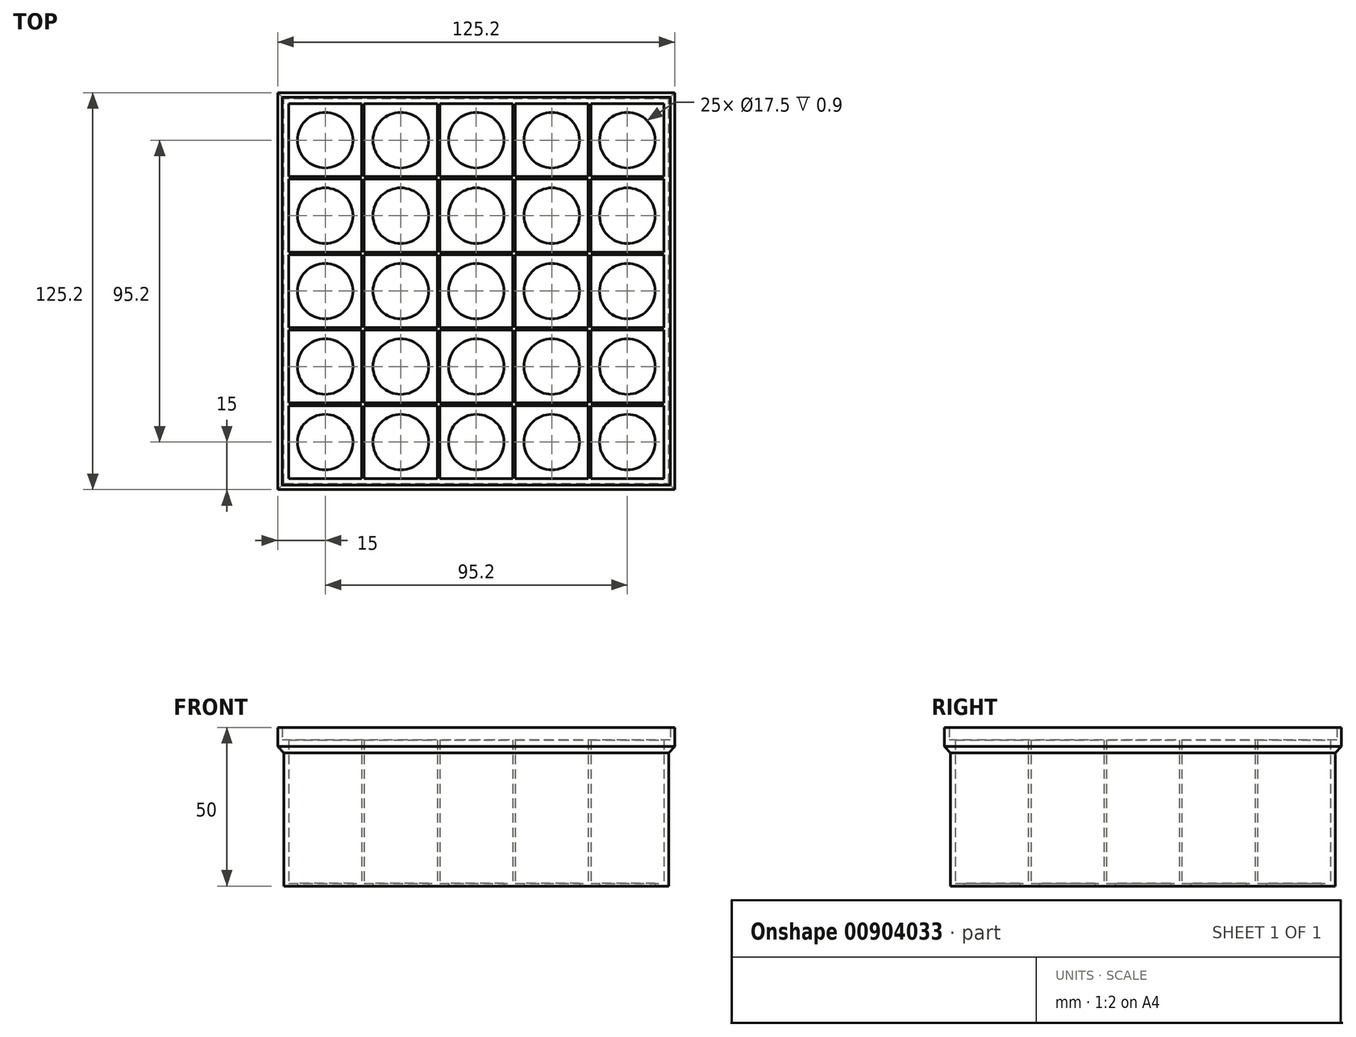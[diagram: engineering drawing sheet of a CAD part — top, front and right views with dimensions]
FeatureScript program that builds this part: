
annotation { "Feature Type Name" : "Feature", "Feature Type Description" : "" }
export const myFeature = defineFeature(function(context is Context, id is Id, definition is map)
    precondition{}
    {
        {
            var Q0;
            Q0=qCreatedBy(makeId("Top.planeOp"),FACE);
            var sketch = newSketch(context, id + "F0", { "sketchPlane" : qUnion([Q0])});
            skLineSegment(sketch, "E0.bottom", {"start": v(-60.6, 60.6) * mm, "end": v(60.6, 60.6) * mm});
            skLineSegment(sketch, "E0.top", {"start": v(-60.6, -60.6) * mm, "end": v(60.6, -60.6) * mm});
            skLineSegment(sketch, "E0.left", {"start": v(-60.6, 60.6) * mm, "end": v(-60.6, -60.6) * mm});
            skLineSegment(sketch, "E0.right", {"start": v(60.6, 60.6) * mm, "end": v(60.6, -60.6) * mm});
            skLineSegment(sketch, "E1", {"start": v(0, 51.44) * mm, "end": v(0, -51.44) * mm, "construction": true});
            skPoint(sketch, "E1.startSnap0", {"position": v(0, 60.6) * mm});
            skPoint(sketch, "E1.endSnap0", {"position": v(0, -60.6) * mm});
            skLineSegment(sketch, "E2", {"start": v(-71.19, 0) * mm, "end": v(76.63, 0) * mm, "construction": true});
            skPoint(sketch, "E2.startSnap0", {"position": v(-60.6, 0) * mm});
            skPoint(sketch, "E3", {"position": v(0, 0) * mm});
            skLineSegment(sketch, "E4", {"start": v(-59.1, 36.1) * mm, "end": v(-36.1, 36.1) * mm});
            skLineSegment(sketch, "E5", {"start": v(-36.1, 36.1) * mm, "end": v(-36.1, 59.1) * mm});
            skLineSegment(sketch, "E6", {"start": v(-59.1, 36.1) * mm, "end": v(-59.1, 59.1) * mm});
            skLineSegment(sketch, "E7", {"start": v(-59.1, 59.1) * mm, "end": v(-36.1, 59.1) * mm});
            skLineSegment(sketch, "E8", {"start": v(-36.1, 47.6) * mm, "end": v(-59.1, 47.6) * mm, "construction": true});
            skLineSegment(sketch, "E9", {"start": v(-47.6, 59.1) * mm, "end": v(-47.6, 36.1) * mm, "construction": true});
            skCircle(sketch, "E10", {"center": v(-47.6, 47.6) * mm, "radius": 8.75 * mm});
            skCircle(sketch, "E11.0.1.0", {"center": v(-47.6, 23.8) * mm, "radius": 8.75 * mm});
            skLineSegment(sketch, "E11.0.1.1", {"start": v(-59.1, 12.3) * mm, "end": v(-59.1, 35.3) * mm});
            skLineSegment(sketch, "E11.0.1.2", {"start": v(-59.1, 12.3) * mm, "end": v(-36.1, 12.3) * mm});
            skLineSegment(sketch, "E11.0.1.3", {"start": v(-59.1, 35.3) * mm, "end": v(-36.1, 35.3) * mm});
            skLineSegment(sketch, "E11.0.1.4", {"start": v(-47.6, 35.3) * mm, "end": v(-47.6, 12.3) * mm, "construction": true});
            skLineSegment(sketch, "E11.0.1.5", {"start": v(-36.1, 23.8) * mm, "end": v(-59.1, 23.8) * mm, "construction": true});
            skLineSegment(sketch, "E11.0.1.6", {"start": v(-36.1, 12.3) * mm, "end": v(-36.1, 35.3) * mm});
            skCircle(sketch, "E11.0.2.0", {"center": v(-47.6, 0) * mm, "radius": 8.75 * mm});
            skLineSegment(sketch, "E11.0.2.1", {"start": v(-59.1, -11.5) * mm, "end": v(-59.1, 11.5) * mm});
            skLineSegment(sketch, "E11.0.2.2", {"start": v(-59.1, -11.5) * mm, "end": v(-36.1, -11.5) * mm});
            skLineSegment(sketch, "E11.0.2.3", {"start": v(-59.1, 11.5) * mm, "end": v(-36.1, 11.5) * mm});
            skLineSegment(sketch, "E11.0.2.4", {"start": v(-47.6, 11.5) * mm, "end": v(-47.6, -11.5) * mm, "construction": true});
            skLineSegment(sketch, "E11.0.2.5", {"start": v(-36.1, 0) * mm, "end": v(-59.1, 0) * mm, "construction": true});
            skLineSegment(sketch, "E11.0.2.6", {"start": v(-36.1, -11.5) * mm, "end": v(-36.1, 11.5) * mm});
            skCircle(sketch, "E11.0.3.0", {"center": v(-47.6, -23.8) * mm, "radius": 8.75 * mm});
            skLineSegment(sketch, "E11.0.3.1", {"start": v(-59.1, -35.3) * mm, "end": v(-59.1, -12.3) * mm});
            skLineSegment(sketch, "E11.0.3.2", {"start": v(-59.1, -35.3) * mm, "end": v(-36.1, -35.3) * mm});
            skLineSegment(sketch, "E11.0.3.3", {"start": v(-59.1, -12.3) * mm, "end": v(-36.1, -12.3) * mm});
            skLineSegment(sketch, "E11.0.3.4", {"start": v(-47.6, -12.3) * mm, "end": v(-47.6, -35.3) * mm, "construction": true});
            skLineSegment(sketch, "E11.0.3.5", {"start": v(-36.1, -23.8) * mm, "end": v(-59.1, -23.8) * mm, "construction": true});
            skLineSegment(sketch, "E11.0.3.6", {"start": v(-36.1, -35.3) * mm, "end": v(-36.1, -12.3) * mm});
            skCircle(sketch, "E11.0.4.0", {"center": v(-47.6, -47.6) * mm, "radius": 8.75 * mm});
            skLineSegment(sketch, "E11.0.4.1", {"start": v(-59.1, -59.1) * mm, "end": v(-59.1, -36.1) * mm});
            skLineSegment(sketch, "E11.0.4.2", {"start": v(-59.1, -59.1) * mm, "end": v(-36.1, -59.1) * mm});
            skLineSegment(sketch, "E11.0.4.3", {"start": v(-59.1, -36.1) * mm, "end": v(-36.1, -36.1) * mm});
            skLineSegment(sketch, "E11.0.4.4", {"start": v(-47.6, -36.1) * mm, "end": v(-47.6, -59.1) * mm, "construction": true});
            skLineSegment(sketch, "E11.0.4.5", {"start": v(-36.1, -47.6) * mm, "end": v(-59.1, -47.6) * mm, "construction": true});
            skLineSegment(sketch, "E11.0.4.6", {"start": v(-36.1, -59.1) * mm, "end": v(-36.1, -36.1) * mm});
            skCircle(sketch, "E11.1.0.0", {"center": v(-23.8, 47.6) * mm, "radius": 8.75 * mm});
            skLineSegment(sketch, "E11.1.0.1", {"start": v(-35.3, 36.1) * mm, "end": v(-35.3, 59.1) * mm});
            skLineSegment(sketch, "E11.1.0.2", {"start": v(-35.3, 36.1) * mm, "end": v(-12.3, 36.1) * mm});
            skLineSegment(sketch, "E11.1.0.3", {"start": v(-35.3, 59.1) * mm, "end": v(-12.3, 59.1) * mm});
            skLineSegment(sketch, "E11.1.0.4", {"start": v(-23.8, 59.1) * mm, "end": v(-23.8, 36.1) * mm, "construction": true});
            skLineSegment(sketch, "E11.1.0.5", {"start": v(-12.3, 47.6) * mm, "end": v(-35.3, 47.6) * mm, "construction": true});
            skLineSegment(sketch, "E11.1.0.6", {"start": v(-12.3, 36.1) * mm, "end": v(-12.3, 59.1) * mm});
            skCircle(sketch, "E11.1.1.0", {"center": v(-23.8, 23.8) * mm, "radius": 8.75 * mm});
            skLineSegment(sketch, "E11.1.1.1", {"start": v(-35.3, 12.3) * mm, "end": v(-35.3, 35.3) * mm});
            skLineSegment(sketch, "E11.1.1.2", {"start": v(-35.3, 12.3) * mm, "end": v(-12.3, 12.3) * mm});
            skLineSegment(sketch, "E11.1.1.3", {"start": v(-35.3, 35.3) * mm, "end": v(-12.3, 35.3) * mm});
            skLineSegment(sketch, "E11.1.1.4", {"start": v(-23.8, 35.3) * mm, "end": v(-23.8, 12.3) * mm, "construction": true});
            skLineSegment(sketch, "E11.1.1.5", {"start": v(-12.3, 23.8) * mm, "end": v(-35.3, 23.8) * mm, "construction": true});
            skLineSegment(sketch, "E11.1.1.6", {"start": v(-12.3, 12.3) * mm, "end": v(-12.3, 35.3) * mm});
            skCircle(sketch, "E11.1.2.0", {"center": v(-23.8, 0) * mm, "radius": 8.75 * mm});
            skLineSegment(sketch, "E11.1.2.1", {"start": v(-35.3, -11.5) * mm, "end": v(-35.3, 11.5) * mm});
            skLineSegment(sketch, "E11.1.2.2", {"start": v(-35.3, -11.5) * mm, "end": v(-12.3, -11.5) * mm});
            skLineSegment(sketch, "E11.1.2.3", {"start": v(-35.3, 11.5) * mm, "end": v(-12.3, 11.5) * mm});
            skLineSegment(sketch, "E11.1.2.4", {"start": v(-23.8, 11.5) * mm, "end": v(-23.8, -11.5) * mm, "construction": true});
            skLineSegment(sketch, "E11.1.2.5", {"start": v(-12.3, 0) * mm, "end": v(-35.3, 0) * mm, "construction": true});
            skLineSegment(sketch, "E11.1.2.6", {"start": v(-12.3, -11.5) * mm, "end": v(-12.3, 11.5) * mm});
            skCircle(sketch, "E11.1.3.0", {"center": v(-23.8, -23.8) * mm, "radius": 8.75 * mm});
            skLineSegment(sketch, "E11.1.3.1", {"start": v(-35.3, -35.3) * mm, "end": v(-35.3, -12.3) * mm});
            skLineSegment(sketch, "E11.1.3.2", {"start": v(-35.3, -35.3) * mm, "end": v(-12.3, -35.3) * mm});
            skLineSegment(sketch, "E11.1.3.3", {"start": v(-35.3, -12.3) * mm, "end": v(-12.3, -12.3) * mm});
            skLineSegment(sketch, "E11.1.3.4", {"start": v(-23.8, -12.3) * mm, "end": v(-23.8, -35.3) * mm, "construction": true});
            skLineSegment(sketch, "E11.1.3.5", {"start": v(-12.3, -23.8) * mm, "end": v(-35.3, -23.8) * mm, "construction": true});
            skLineSegment(sketch, "E11.1.3.6", {"start": v(-12.3, -35.3) * mm, "end": v(-12.3, -12.3) * mm});
            skCircle(sketch, "E11.1.4.0", {"center": v(-23.8, -47.6) * mm, "radius": 8.75 * mm});
            skLineSegment(sketch, "E11.1.4.1", {"start": v(-35.3, -59.1) * mm, "end": v(-35.3, -36.1) * mm});
            skLineSegment(sketch, "E11.1.4.2", {"start": v(-35.3, -59.1) * mm, "end": v(-12.3, -59.1) * mm});
            skLineSegment(sketch, "E11.1.4.3", {"start": v(-35.3, -36.1) * mm, "end": v(-12.3, -36.1) * mm});
            skLineSegment(sketch, "E11.1.4.4", {"start": v(-23.8, -36.1) * mm, "end": v(-23.8, -59.1) * mm, "construction": true});
            skLineSegment(sketch, "E11.1.4.5", {"start": v(-12.3, -47.6) * mm, "end": v(-35.3, -47.6) * mm, "construction": true});
            skLineSegment(sketch, "E11.1.4.6", {"start": v(-12.3, -59.1) * mm, "end": v(-12.3, -36.1) * mm});
            skCircle(sketch, "E11.2.0.0", {"center": v(0, 47.6) * mm, "radius": 8.75 * mm});
            skLineSegment(sketch, "E11.2.0.1", {"start": v(-11.5, 36.1) * mm, "end": v(-11.5, 59.1) * mm});
            skLineSegment(sketch, "E11.2.0.2", {"start": v(-11.5, 36.1) * mm, "end": v(11.5, 36.1) * mm});
            skLineSegment(sketch, "E11.2.0.3", {"start": v(-11.5, 59.1) * mm, "end": v(11.5, 59.1) * mm});
            skLineSegment(sketch, "E11.2.0.4", {"start": v(0, 59.1) * mm, "end": v(0, 36.1) * mm, "construction": true});
            skLineSegment(sketch, "E11.2.0.5", {"start": v(11.5, 47.6) * mm, "end": v(-11.5, 47.6) * mm, "construction": true});
            skLineSegment(sketch, "E11.2.0.6", {"start": v(11.5, 36.1) * mm, "end": v(11.5, 59.1) * mm});
            skCircle(sketch, "E11.2.1.0", {"center": v(0, 23.8) * mm, "radius": 8.75 * mm});
            skLineSegment(sketch, "E11.2.1.1", {"start": v(-11.5, 12.3) * mm, "end": v(-11.5, 35.3) * mm});
            skLineSegment(sketch, "E11.2.1.2", {"start": v(-11.5, 12.3) * mm, "end": v(11.5, 12.3) * mm});
            skLineSegment(sketch, "E11.2.1.3", {"start": v(-11.5, 35.3) * mm, "end": v(11.5, 35.3) * mm});
            skLineSegment(sketch, "E11.2.1.4", {"start": v(0, 35.3) * mm, "end": v(0, 12.3) * mm, "construction": true});
            skLineSegment(sketch, "E11.2.1.5", {"start": v(11.5, 23.8) * mm, "end": v(-11.5, 23.8) * mm, "construction": true});
            skLineSegment(sketch, "E11.2.1.6", {"start": v(11.5, 12.3) * mm, "end": v(11.5, 35.3) * mm});
            skCircle(sketch, "E11.2.2.0", {"center": v(0, 0) * mm, "radius": 8.75 * mm});
            skLineSegment(sketch, "E11.2.2.1", {"start": v(-11.5, -11.5) * mm, "end": v(-11.5, 11.5) * mm});
            skLineSegment(sketch, "E11.2.2.2", {"start": v(-11.5, -11.5) * mm, "end": v(11.5, -11.5) * mm});
            skLineSegment(sketch, "E11.2.2.3", {"start": v(-11.5, 11.5) * mm, "end": v(11.5, 11.5) * mm});
            skLineSegment(sketch, "E11.2.2.4", {"start": v(0, 11.5) * mm, "end": v(0, -11.5) * mm, "construction": true});
            skLineSegment(sketch, "E11.2.2.5", {"start": v(11.5, 0) * mm, "end": v(-11.5, 0) * mm, "construction": true});
            skLineSegment(sketch, "E11.2.2.6", {"start": v(11.5, -11.5) * mm, "end": v(11.5, 11.5) * mm});
            skCircle(sketch, "E11.2.3.0", {"center": v(0, -23.8) * mm, "radius": 8.75 * mm});
            skLineSegment(sketch, "E11.2.3.1", {"start": v(-11.5, -35.3) * mm, "end": v(-11.5, -12.3) * mm});
            skLineSegment(sketch, "E11.2.3.2", {"start": v(-11.5, -35.3) * mm, "end": v(11.5, -35.3) * mm});
            skLineSegment(sketch, "E11.2.3.3", {"start": v(-11.5, -12.3) * mm, "end": v(11.5, -12.3) * mm});
            skLineSegment(sketch, "E11.2.3.4", {"start": v(0, -12.3) * mm, "end": v(0, -35.3) * mm, "construction": true});
            skLineSegment(sketch, "E11.2.3.5", {"start": v(11.5, -23.8) * mm, "end": v(-11.5, -23.8) * mm, "construction": true});
            skLineSegment(sketch, "E11.2.3.6", {"start": v(11.5, -35.3) * mm, "end": v(11.5, -12.3) * mm});
            skCircle(sketch, "E11.2.4.0", {"center": v(0, -47.6) * mm, "radius": 8.75 * mm});
            skLineSegment(sketch, "E11.2.4.1", {"start": v(-11.5, -59.1) * mm, "end": v(-11.5, -36.1) * mm});
            skLineSegment(sketch, "E11.2.4.2", {"start": v(-11.5, -59.1) * mm, "end": v(11.5, -59.1) * mm});
            skLineSegment(sketch, "E11.2.4.3", {"start": v(-11.5, -36.1) * mm, "end": v(11.5, -36.1) * mm});
            skLineSegment(sketch, "E11.2.4.4", {"start": v(0, -36.1) * mm, "end": v(0, -59.1) * mm, "construction": true});
            skLineSegment(sketch, "E11.2.4.5", {"start": v(11.5, -47.6) * mm, "end": v(-11.5, -47.6) * mm, "construction": true});
            skLineSegment(sketch, "E11.2.4.6", {"start": v(11.5, -59.1) * mm, "end": v(11.5, -36.1) * mm});
            skCircle(sketch, "E11.3.0.0", {"center": v(23.8, 47.6) * mm, "radius": 8.75 * mm});
            skLineSegment(sketch, "E11.3.0.1", {"start": v(12.3, 36.1) * mm, "end": v(12.3, 59.1) * mm});
            skLineSegment(sketch, "E11.3.0.2", {"start": v(12.3, 36.1) * mm, "end": v(35.3, 36.1) * mm});
            skLineSegment(sketch, "E11.3.0.3", {"start": v(12.3, 59.1) * mm, "end": v(35.3, 59.1) * mm});
            skLineSegment(sketch, "E11.3.0.4", {"start": v(23.8, 59.1) * mm, "end": v(23.8, 36.1) * mm, "construction": true});
            skLineSegment(sketch, "E11.3.0.5", {"start": v(35.3, 47.6) * mm, "end": v(12.3, 47.6) * mm, "construction": true});
            skLineSegment(sketch, "E11.3.0.6", {"start": v(35.3, 36.1) * mm, "end": v(35.3, 59.1) * mm});
            skCircle(sketch, "E11.3.1.0", {"center": v(23.8, 23.8) * mm, "radius": 8.75 * mm});
            skLineSegment(sketch, "E11.3.1.1", {"start": v(12.3, 12.3) * mm, "end": v(12.3, 35.3) * mm});
            skLineSegment(sketch, "E11.3.1.2", {"start": v(12.3, 12.3) * mm, "end": v(35.3, 12.3) * mm});
            skLineSegment(sketch, "E11.3.1.3", {"start": v(12.3, 35.3) * mm, "end": v(35.3, 35.3) * mm});
            skLineSegment(sketch, "E11.3.1.4", {"start": v(23.8, 35.3) * mm, "end": v(23.8, 12.3) * mm, "construction": true});
            skLineSegment(sketch, "E11.3.1.5", {"start": v(35.3, 23.8) * mm, "end": v(12.3, 23.8) * mm, "construction": true});
            skLineSegment(sketch, "E11.3.1.6", {"start": v(35.3, 12.3) * mm, "end": v(35.3, 35.3) * mm});
            skCircle(sketch, "E11.3.2.0", {"center": v(23.8, 0) * mm, "radius": 8.75 * mm});
            skLineSegment(sketch, "E11.3.2.1", {"start": v(12.3, -11.5) * mm, "end": v(12.3, 11.5) * mm});
            skLineSegment(sketch, "E11.3.2.2", {"start": v(12.3, -11.5) * mm, "end": v(35.3, -11.5) * mm});
            skLineSegment(sketch, "E11.3.2.3", {"start": v(12.3, 11.5) * mm, "end": v(35.3, 11.5) * mm});
            skLineSegment(sketch, "E11.3.2.4", {"start": v(23.8, 11.5) * mm, "end": v(23.8, -11.5) * mm, "construction": true});
            skLineSegment(sketch, "E11.3.2.5", {"start": v(35.3, 0) * mm, "end": v(12.3, 0) * mm, "construction": true});
            skLineSegment(sketch, "E11.3.2.6", {"start": v(35.3, -11.5) * mm, "end": v(35.3, 11.5) * mm});
            skCircle(sketch, "E11.3.3.0", {"center": v(23.8, -23.8) * mm, "radius": 8.75 * mm});
            skLineSegment(sketch, "E11.3.3.1", {"start": v(12.3, -35.3) * mm, "end": v(12.3, -12.3) * mm});
            skLineSegment(sketch, "E11.3.3.2", {"start": v(12.3, -35.3) * mm, "end": v(35.3, -35.3) * mm});
            skLineSegment(sketch, "E11.3.3.3", {"start": v(12.3, -12.3) * mm, "end": v(35.3, -12.3) * mm});
            skLineSegment(sketch, "E11.3.3.4", {"start": v(23.8, -12.3) * mm, "end": v(23.8, -35.3) * mm, "construction": true});
            skLineSegment(sketch, "E11.3.3.5", {"start": v(35.3, -23.8) * mm, "end": v(12.3, -23.8) * mm, "construction": true});
            skLineSegment(sketch, "E11.3.3.6", {"start": v(35.3, -35.3) * mm, "end": v(35.3, -12.3) * mm});
            skCircle(sketch, "E11.3.4.0", {"center": v(23.8, -47.6) * mm, "radius": 8.75 * mm});
            skLineSegment(sketch, "E11.3.4.1", {"start": v(12.3, -59.1) * mm, "end": v(12.3, -36.1) * mm});
            skLineSegment(sketch, "E11.3.4.2", {"start": v(12.3, -59.1) * mm, "end": v(35.3, -59.1) * mm});
            skLineSegment(sketch, "E11.3.4.3", {"start": v(12.3, -36.1) * mm, "end": v(35.3, -36.1) * mm});
            skLineSegment(sketch, "E11.3.4.4", {"start": v(23.8, -36.1) * mm, "end": v(23.8, -59.1) * mm, "construction": true});
            skLineSegment(sketch, "E11.3.4.5", {"start": v(35.3, -47.6) * mm, "end": v(12.3, -47.6) * mm, "construction": true});
            skLineSegment(sketch, "E11.3.4.6", {"start": v(35.3, -59.1) * mm, "end": v(35.3, -36.1) * mm});
            skCircle(sketch, "E11.4.0.0", {"center": v(47.6, 47.6) * mm, "radius": 8.75 * mm});
            skLineSegment(sketch, "E11.4.0.1", {"start": v(36.1, 36.1) * mm, "end": v(36.1, 59.1) * mm});
            skLineSegment(sketch, "E11.4.0.2", {"start": v(36.1, 36.1) * mm, "end": v(59.1, 36.1) * mm});
            skLineSegment(sketch, "E11.4.0.3", {"start": v(36.1, 59.1) * mm, "end": v(59.1, 59.1) * mm});
            skLineSegment(sketch, "E11.4.0.4", {"start": v(47.6, 59.1) * mm, "end": v(47.6, 36.1) * mm, "construction": true});
            skLineSegment(sketch, "E11.4.0.5", {"start": v(59.1, 47.6) * mm, "end": v(36.1, 47.6) * mm, "construction": true});
            skLineSegment(sketch, "E11.4.0.6", {"start": v(59.1, 36.1) * mm, "end": v(59.1, 59.1) * mm});
            skCircle(sketch, "E11.4.1.0", {"center": v(47.6, 23.8) * mm, "radius": 8.75 * mm});
            skLineSegment(sketch, "E11.4.1.1", {"start": v(36.1, 12.3) * mm, "end": v(36.1, 35.3) * mm});
            skLineSegment(sketch, "E11.4.1.2", {"start": v(36.1, 12.3) * mm, "end": v(59.1, 12.3) * mm});
            skLineSegment(sketch, "E11.4.1.3", {"start": v(36.1, 35.3) * mm, "end": v(59.1, 35.3) * mm});
            skLineSegment(sketch, "E11.4.1.4", {"start": v(47.6, 35.3) * mm, "end": v(47.6, 12.3) * mm, "construction": true});
            skLineSegment(sketch, "E11.4.1.5", {"start": v(59.1, 23.8) * mm, "end": v(36.1, 23.8) * mm, "construction": true});
            skLineSegment(sketch, "E11.4.1.6", {"start": v(59.1, 12.3) * mm, "end": v(59.1, 35.3) * mm});
            skCircle(sketch, "E11.4.2.0", {"center": v(47.6, 0) * mm, "radius": 8.75 * mm});
            skLineSegment(sketch, "E11.4.2.1", {"start": v(36.1, -11.5) * mm, "end": v(36.1, 11.5) * mm});
            skLineSegment(sketch, "E11.4.2.2", {"start": v(36.1, -11.5) * mm, "end": v(59.1, -11.5) * mm});
            skLineSegment(sketch, "E11.4.2.3", {"start": v(36.1, 11.5) * mm, "end": v(59.1, 11.5) * mm});
            skLineSegment(sketch, "E11.4.2.4", {"start": v(47.6, 11.5) * mm, "end": v(47.6, -11.5) * mm, "construction": true});
            skLineSegment(sketch, "E11.4.2.5", {"start": v(59.1, 0) * mm, "end": v(36.1, 0) * mm, "construction": true});
            skLineSegment(sketch, "E11.4.2.6", {"start": v(59.1, -11.5) * mm, "end": v(59.1, 11.5) * mm});
            skCircle(sketch, "E11.4.3.0", {"center": v(47.6, -23.8) * mm, "radius": 8.75 * mm});
            skLineSegment(sketch, "E11.4.3.1", {"start": v(36.1, -35.3) * mm, "end": v(36.1, -12.3) * mm});
            skLineSegment(sketch, "E11.4.3.2", {"start": v(36.1, -35.3) * mm, "end": v(59.1, -35.3) * mm});
            skLineSegment(sketch, "E11.4.3.3", {"start": v(36.1, -12.3) * mm, "end": v(59.1, -12.3) * mm});
            skLineSegment(sketch, "E11.4.3.4", {"start": v(47.6, -12.3) * mm, "end": v(47.6, -35.3) * mm, "construction": true});
            skLineSegment(sketch, "E11.4.3.5", {"start": v(59.1, -23.8) * mm, "end": v(36.1, -23.8) * mm, "construction": true});
            skLineSegment(sketch, "E11.4.3.6", {"start": v(59.1, -35.3) * mm, "end": v(59.1, -12.3) * mm});
            skCircle(sketch, "E11.4.4.0", {"center": v(47.6, -47.6) * mm, "radius": 8.75 * mm});
            skLineSegment(sketch, "E11.4.4.1", {"start": v(36.1, -59.1) * mm, "end": v(36.1, -36.1) * mm});
            skLineSegment(sketch, "E11.4.4.2", {"start": v(36.1, -59.1) * mm, "end": v(59.1, -59.1) * mm});
            skLineSegment(sketch, "E11.4.4.3", {"start": v(36.1, -36.1) * mm, "end": v(59.1, -36.1) * mm});
            skLineSegment(sketch, "E11.4.4.4", {"start": v(47.6, -36.1) * mm, "end": v(47.6, -59.1) * mm, "construction": true});
            skLineSegment(sketch, "E11.4.4.5", {"start": v(59.1, -47.6) * mm, "end": v(36.1, -47.6) * mm, "construction": true});
            skLineSegment(sketch, "E11.4.4.6", {"start": v(59.1, -59.1) * mm, "end": v(59.1, -36.1) * mm});
            skLineSegment(sketch, "E11.direction1", {"start": v(-59.1, 36.1) * mm, "end": v(-35.3, 36.1) * mm, "construction": true});
            skLineSegment(sketch, "E11.direction2", {"start": v(-59.1, 36.1) * mm, "end": v(-59.1, 12.3) * mm, "construction": true});
            skLineSegment(sketch, "E12", {"start": v(-59.1, 36.1) * mm, "end": v(-59.1, 35.3) * mm});
            skLineSegment(sketch, "E13", {"start": v(-59.1, 12.3) * mm, "end": v(-59.1, 11.5) * mm});
            skLineSegment(sketch, "E14", {"start": v(-59.1, -11.5) * mm, "end": v(-59.1, -12.3) * mm});
            skLineSegment(sketch, "E15", {"start": v(-59.1, -35.3) * mm, "end": v(-59.1, -36.1) * mm});
            skLineSegment(sketch, "E16", {"start": v(-36.1, -59.1) * mm, "end": v(-35.3, -59.1) * mm});
            skLineSegment(sketch, "E17", {"start": v(-12.3, -59.1) * mm, "end": v(-11.5, -59.1) * mm});
            skLineSegment(sketch, "E18", {"start": v(11.5, -59.1) * mm, "end": v(12.3, -59.1) * mm});
            skLineSegment(sketch, "E19", {"start": v(35.3, -59.1) * mm, "end": v(36.1, -59.1) * mm});
            skLineSegment(sketch, "E20", {"start": v(59.1, -36.1) * mm, "end": v(59.1, -35.3) * mm});
            skLineSegment(sketch, "E21", {"start": v(59.1, -12.3) * mm, "end": v(59.1, -11.5) * mm});
            skLineSegment(sketch, "E22", {"start": v(59.1, 11.5) * mm, "end": v(59.1, 12.3) * mm});
            skLineSegment(sketch, "E23", {"start": v(59.1, 35.3) * mm, "end": v(59.1, 36.1) * mm});
            skLineSegment(sketch, "E24", {"start": v(35.3, 59.1) * mm, "end": v(36.1, 59.1) * mm});
            skLineSegment(sketch, "E25", {"start": v(11.5, 59.1) * mm, "end": v(12.3, 59.1) * mm});
            skLineSegment(sketch, "E26", {"start": v(-12.3, 59.1) * mm, "end": v(-11.5, 59.1) * mm});
            skLineSegment(sketch, "E27", {"start": v(-36.1, 59.1) * mm, "end": v(-35.3, 59.1) * mm});
            skSolve(sketch);
        }
        {
            var Q0;
            Q0=makeQuery(id+"F0.imprint","IMPRINT",FACE,{"disambiguationData":[TD([[makeQuery(id+"F0.imprint","IMPRINT",EDGE,{"derivedFrom":sQuery(id+"F0.wireOp",EDGE,"E4")}),-1.0]])]});
            var Q1;
            Q1=makeQuery(id+"F0.imprint","IMPRINT",FACE,{"disambiguationData":[TD([[makeQuery(id+"F0.imprint","IMPRINT",EDGE,{"derivedFrom":sQuery(id+"F0.wireOp",EDGE,"E0.bottom")}),-1.0]])]});
            extrude(context, id + "F1", {"entities" : qUnion([Q0, Q1]), "depth" : 46 * mm, "offsetDistance" : 25 * mm});
        }
        {
            var Q0;
            Q0=makeQuery(id+"F0.imprint","IMPRINT",FACE,{"disambiguationData":[TD([[makeQuery(id+"F0.imprint","IMPRINT",EDGE,{"derivedFrom":sQuery(id+"F0.wireOp",EDGE,"E4")}),1.0]])]});
            var Q1;
            Q1=makeQuery(id+"F0.imprint","IMPRINT",FACE,{"disambiguationData":[TD([[makeQuery(id+"F0.imprint","IMPRINT",EDGE,{"derivedFrom":sQuery(id+"F0.wireOp",EDGE,"E11.1.0.0")}),-1.0]])]});
            var Q2;
            Q2=makeQuery(id+"F0.imprint","IMPRINT",FACE,{"disambiguationData":[TD([[makeQuery(id+"F0.imprint","IMPRINT",EDGE,{"derivedFrom":sQuery(id+"F0.wireOp",EDGE,"E11.2.0.0")}),-1.0]])]});
            var Q3;
            Q3=makeQuery(id+"F0.imprint","IMPRINT",FACE,{"disambiguationData":[TD([[makeQuery(id+"F0.imprint","IMPRINT",EDGE,{"derivedFrom":sQuery(id+"F0.wireOp",EDGE,"E11.3.0.0")}),-1.0]])]});
            var Q4;
            Q4=makeQuery(id+"F0.imprint","IMPRINT",FACE,{"disambiguationData":[TD([[makeQuery(id+"F0.imprint","IMPRINT",EDGE,{"derivedFrom":sQuery(id+"F0.wireOp",EDGE,"E11.4.0.0")}),-1.0]])]});
            var Q5;
            Q5=makeQuery(id+"F0.imprint","IMPRINT",FACE,{"disambiguationData":[TD([[makeQuery(id+"F0.imprint","IMPRINT",EDGE,{"derivedFrom":sQuery(id+"F0.wireOp",EDGE,"E11.4.1.0")}),-1.0]])]});
            var Q6;
            Q6=makeQuery(id+"F0.imprint","IMPRINT",FACE,{"disambiguationData":[TD([[makeQuery(id+"F0.imprint","IMPRINT",EDGE,{"derivedFrom":sQuery(id+"F0.wireOp",EDGE,"E11.3.1.0")}),-1.0]])]});
            var Q7;
            Q7=makeQuery(id+"F0.imprint","IMPRINT",FACE,{"disambiguationData":[TD([[makeQuery(id+"F0.imprint","IMPRINT",EDGE,{"derivedFrom":sQuery(id+"F0.wireOp",EDGE,"E11.2.1.0")}),-1.0]])]});
            var Q8;
            Q8=makeQuery(id+"F0.imprint","IMPRINT",FACE,{"disambiguationData":[TD([[makeQuery(id+"F0.imprint","IMPRINT",EDGE,{"derivedFrom":sQuery(id+"F0.wireOp",EDGE,"E11.1.1.0")}),-1.0]])]});
            var Q9;
            Q9=makeQuery(id+"F0.imprint","IMPRINT",FACE,{"disambiguationData":[TD([[makeQuery(id+"F0.imprint","IMPRINT",EDGE,{"derivedFrom":sQuery(id+"F0.wireOp",EDGE,"E11.0.1.0")}),-1.0]])]});
            var Q10;
            Q10=makeQuery(id+"F0.imprint","IMPRINT",FACE,{"disambiguationData":[TD([[makeQuery(id+"F0.imprint","IMPRINT",EDGE,{"derivedFrom":sQuery(id+"F0.wireOp",EDGE,"E11.0.2.0")}),-1.0]])]});
            var Q11;
            Q11=makeQuery(id+"F0.imprint","IMPRINT",FACE,{"disambiguationData":[TD([[makeQuery(id+"F0.imprint","IMPRINT",EDGE,{"derivedFrom":sQuery(id+"F0.wireOp",EDGE,"E11.1.2.0")}),-1.0]])]});
            var Q12;
            Q12=makeQuery(id+"F0.imprint","IMPRINT",FACE,{"disambiguationData":[TD([[makeQuery(id+"F0.imprint","IMPRINT",EDGE,{"derivedFrom":sQuery(id+"F0.wireOp",EDGE,"E11.2.2.0")}),-1.0]])]});
            var Q13;
            Q13=makeQuery(id+"F0.imprint","IMPRINT",FACE,{"disambiguationData":[TD([[makeQuery(id+"F0.imprint","IMPRINT",EDGE,{"derivedFrom":sQuery(id+"F0.wireOp",EDGE,"E11.3.2.0")}),-1.0]])]});
            var Q14;
            Q14=makeQuery(id+"F0.imprint","IMPRINT",FACE,{"disambiguationData":[TD([[makeQuery(id+"F0.imprint","IMPRINT",EDGE,{"derivedFrom":sQuery(id+"F0.wireOp",EDGE,"E11.4.2.0")}),-1.0]])]});
            var Q15;
            Q15=makeQuery(id+"F0.imprint","IMPRINT",FACE,{"disambiguationData":[TD([[makeQuery(id+"F0.imprint","IMPRINT",EDGE,{"derivedFrom":sQuery(id+"F0.wireOp",EDGE,"E11.4.3.0")}),-1.0]])]});
            var Q16;
            Q16=makeQuery(id+"F0.imprint","IMPRINT",FACE,{"disambiguationData":[TD([[makeQuery(id+"F0.imprint","IMPRINT",EDGE,{"derivedFrom":sQuery(id+"F0.wireOp",EDGE,"E11.3.3.0")}),-1.0]])]});
            var Q17;
            Q17=makeQuery(id+"F0.imprint","IMPRINT",FACE,{"disambiguationData":[TD([[makeQuery(id+"F0.imprint","IMPRINT",EDGE,{"derivedFrom":sQuery(id+"F0.wireOp",EDGE,"E11.2.3.0")}),-1.0]])]});
            var Q18;
            Q18=makeQuery(id+"F0.imprint","IMPRINT",FACE,{"disambiguationData":[TD([[makeQuery(id+"F0.imprint","IMPRINT",EDGE,{"derivedFrom":sQuery(id+"F0.wireOp",EDGE,"E11.1.3.0")}),-1.0]])]});
            var Q19;
            Q19=makeQuery(id+"F0.imprint","IMPRINT",FACE,{"disambiguationData":[TD([[makeQuery(id+"F0.imprint","IMPRINT",EDGE,{"derivedFrom":sQuery(id+"F0.wireOp",EDGE,"E11.0.3.0")}),-1.0]])]});
            var Q20;
            Q20=makeQuery(id+"F0.imprint","IMPRINT",FACE,{"disambiguationData":[TD([[makeQuery(id+"F0.imprint","IMPRINT",EDGE,{"derivedFrom":sQuery(id+"F0.wireOp",EDGE,"E11.0.4.0")}),-1.0]])]});
            var Q21;
            Q21=makeQuery(id+"F0.imprint","IMPRINT",FACE,{"disambiguationData":[TD([[makeQuery(id+"F0.imprint","IMPRINT",EDGE,{"derivedFrom":sQuery(id+"F0.wireOp",EDGE,"E11.1.4.0")}),-1.0]])]});
            var Q22;
            Q22=makeQuery(id+"F0.imprint","IMPRINT",FACE,{"disambiguationData":[TD([[makeQuery(id+"F0.imprint","IMPRINT",EDGE,{"derivedFrom":sQuery(id+"F0.wireOp",EDGE,"E11.2.4.0")}),-1.0]])]});
            var Q23;
            Q23=makeQuery(id+"F0.imprint","IMPRINT",FACE,{"disambiguationData":[TD([[makeQuery(id+"F0.imprint","IMPRINT",EDGE,{"derivedFrom":sQuery(id+"F0.wireOp",EDGE,"E11.3.4.0")}),-1.0]])]});
            var Q24;
            Q24=makeQuery(id+"F0.imprint","IMPRINT",FACE,{"disambiguationData":[TD([[makeQuery(id+"F0.imprint","IMPRINT",EDGE,{"derivedFrom":sQuery(id+"F0.wireOp",EDGE,"E11.4.4.0")}),-1.0]])]});
            extrude(context, id + "F2", {"entities" : qUnion([Q0, Q1, Q2, Q3, Q4, Q5, Q6, Q7, Q8, Q9, Q10, Q11, Q12, Q13, Q14, Q15, Q16, Q17, Q18, Q19, Q20, Q21, Q22, Q23, Q24]), "operationType" : NewBodyOperationType.ADD, "depth" : 0.9 * mm, "offsetDistance" : 25 * mm});
        }
        {
            var Q0;
            Q0=makeQuery(id+"F1.opExtrude","SWEPT_FACE",FACE,{"disambiguationData":[OSD([sQuery(id+"F0.wireOp",EDGE,"E0.left")])]});
            var sketch = newSketch(context, id + "F3", { "sketchPlane" : qUnion([Q0])});
            skLineSegment(sketch, "E28", {"start": v(-60.6, 46) * mm, "end": v(60.6, 46) * mm});
            skLineSegment(sketch, "E29", {"start": v(60.6, 46) * mm, "end": v(60.6, 42) * mm});
            skLineSegment(sketch, "E30", {"start": v(60.6, 42) * mm, "end": v(-60.6, 42) * mm});
            skLineSegment(sketch, "E31", {"start": v(-60.6, 42) * mm, "end": v(-60.6, 46) * mm});
            skSolve(sketch);
        }
        {
            var Q0;
            {var subQ2=sQuery(id+"F3.wireOp",EDGE,"SVkf91RX-VQeT-ybFR-xyFN-Pj7coNB4GysW");Q0=makeQuery(id+"F3.imprint","IMPRINT",FACE,{"disambiguationData":[TD([[makeQuery(id+"F3.imprint","IMPRINT",EDGE,{"derivedFrom":subQ2}),-1.0]])]});}
            var Q1;
            {var subQ3=sQuery(id+"F3.wireOp",EDGE,"bE7k9VMM-xArz-5oJY-kQJE-XANRKUG4KspI");Q1=makeQuery(id+"F3.imprint","IMPRINT",FACE,{"disambiguationData":[TD([[makeQuery(id+"F3.imprint","IMPRINT",EDGE,{"derivedFrom":subQ3}),-1.0]])]});}
            var Q2;
            Q2=makeQuery(id+"F3.imprint","IMPRINT",FACE,{"disambiguationData":[TD([[makeQuery(id+"F3.imprint","IMPRINT",EDGE,{"derivedFrom":sQuery(id+"F3.wireOp",EDGE,"E28")}),-1.0]])]});
            extrude(context, id + "F4", {"entities" : qUnion([Q0, Q1, Q2]), "operationType" : NewBodyOperationType.ADD, "depth" : 2 * mm, "offsetDistance" : 25 * mm});
        }
        {
            var Q0;
            Q0=makeQuery(id+"F4.opExtrude","CAP_EDGE",EDGE,{"disambiguationData":[OSD([sQuery(id+"F3.wireOp",EDGE,"E30")])],"isStart":false});
            chamfer(context, id + "F5", {"entities" : qUnion([Q0]), "width" : 2 * mm, "tangentPropagation" : true});
        }
        {
            var Q0;
            Q0=makeQuery(id+"F4.boolean.opBoolean","MERGE",FACE,{"derivedFrom":[makeQuery(id+"F1.opExtrude","SWEPT_FACE",FACE,{"disambiguationData":[OSD([sQuery(id+"F0.wireOp",EDGE,"E0.top")])]}),makeQuery(id+"F4.opExtrude","SWEPT_FACE",FACE,{"disambiguationData":[OSD([sQuery(id+"F3.wireOp",EDGE,"E29")])]})]});
            var sketch = newSketch(context, id + "F6", { "sketchPlane" : qUnion([Q0])});
            skLineSegment(sketch, "E32", {"start": v(-60.6, 42) * mm, "end": v(60.6, 42) * mm});
            skLineSegment(sketch, "E33", {"start": v(60.6, 42) * mm, "end": v(60.6, 46) * mm});
            skLineSegment(sketch, "E34", {"start": v(60.6, 46) * mm, "end": v(-62.6, 46) * mm});
            skLineSegment(sketch, "E35", {"start": v(-62.6, 46) * mm, "end": v(-62.6, 44) * mm});
            skLineSegment(sketch, "E36", {"start": v(-62.6, 44) * mm, "end": v(-60.6, 42) * mm});
            skSolve(sketch);
        }
        {
            var Q0;
            Q0=makeQuery(id+"F6.imprint","IMPRINT",FACE,{"disambiguationData":[TD([[makeQuery(id+"F6.imprint","IMPRINT",EDGE,{"derivedFrom":sQuery(id+"F6.wireOp",EDGE,"E32")}),1.0]])]});
            extrude(context, id + "F7", {"entities" : qUnion([Q0]), "operationType" : NewBodyOperationType.ADD, "depth" : 2 * mm, "offsetDistance" : 25 * mm});
        }
        {
            var Q0;
            Q0=makeQuery(id+"F7.opExtrude","CAP_EDGE",EDGE,{"disambiguationData":[OSD([sQuery(id+"F6.wireOp",EDGE,"E32")])],"isStart":false});
            chamfer(context, id + "F8", {"entities" : qUnion([Q0]), "width" : 2 * mm, "tangentPropagation" : true});
        }
        {
            var Q0;
            Q0=makeQuery(id+"F7.boolean.opBoolean","MERGE",FACE,{"derivedFrom":[makeQuery(id+"F1.opExtrude","SWEPT_FACE",FACE,{"disambiguationData":[OSD([sQuery(id+"F0.wireOp",EDGE,"E0.right")])]}),makeQuery(id+"F7.opExtrude","SWEPT_FACE",FACE,{"disambiguationData":[OSD([sQuery(id+"F6.wireOp",EDGE,"E33")])]})]});
            var sketch = newSketch(context, id + "F9", { "sketchPlane" : qUnion([Q0])});
            skLineSegment(sketch, "E37", {"start": v(60.6, 46) * mm, "end": v(-62.6, 46) * mm});
            skLineSegment(sketch, "E38", {"start": v(-62.6, 46) * mm, "end": v(-62.6, 44) * mm});
            skLineSegment(sketch, "E39", {"start": v(-62.6, 44) * mm, "end": v(-60.6, 42) * mm});
            skLineSegment(sketch, "E40", {"start": v(-60.6, 42) * mm, "end": v(60.6, 42) * mm});
            skLineSegment(sketch, "E41", {"start": v(60.6, 42) * mm, "end": v(60.6, 46) * mm});
            skSolve(sketch);
        }
        {
            var Q0;
            Q0=makeQuery(id+"F9.imprint","IMPRINT",FACE,{"disambiguationData":[TD([[makeQuery(id+"F9.imprint","IMPRINT",EDGE,{"derivedFrom":sQuery(id+"F9.wireOp",EDGE,"E37")}),1.0]])]});
            extrude(context, id + "F10", {"entities" : qUnion([Q0]), "operationType" : NewBodyOperationType.ADD, "depth" : 2 * mm, "offsetDistance" : 25 * mm});
        }
        {
            var Q0;
            Q0=makeQuery(id+"F10.opExtrude","CAP_EDGE",EDGE,{"disambiguationData":[OSD([sQuery(id+"F9.wireOp",EDGE,"E40")])],"isStart":false});
            chamfer(context, id + "F11", {"entities" : qUnion([Q0]), "width" : 2 * mm, "tangentPropagation" : true});
        }
        {
            var Q0;
            Q0=makeQuery(id+"F10.boolean.opBoolean","MERGE",FACE,{"derivedFrom":[makeQuery(id+"F4.boolean.opBoolean","MERGE",FACE,{"derivedFrom":[makeQuery(id+"F1.opExtrude","SWEPT_FACE",FACE,{"disambiguationData":[OSD([sQuery(id+"F0.wireOp",EDGE,"E0.bottom")])]}),makeQuery(id+"F4.opExtrude","SWEPT_FACE",FACE,{"disambiguationData":[OSD([sQuery(id+"F3.wireOp",EDGE,"E31")])]})]}),makeQuery(id+"F10.opExtrude","SWEPT_FACE",FACE,{"disambiguationData":[OSD([sQuery(id+"F9.wireOp",EDGE,"E41")])]})]});
            var sketch = newSketch(context, id + "F12", { "sketchPlane" : qUnion([Q0])});
            skLineSegment(sketch, "E42", {"start": v(62.6, 46) * mm, "end": v(-62.6, 46) * mm});
            skLineSegment(sketch, "E43", {"start": v(-62.6, 46) * mm, "end": v(-62.6, 44) * mm});
            skLineSegment(sketch, "E44", {"start": v(-62.6, 44) * mm, "end": v(-60.6, 42) * mm});
            skLineSegment(sketch, "E45", {"start": v(-60.6, 42) * mm, "end": v(60.6, 42) * mm});
            skLineSegment(sketch, "E46", {"start": v(60.6, 42) * mm, "end": v(62.6, 44) * mm});
            skLineSegment(sketch, "E47", {"start": v(62.6, 44) * mm, "end": v(62.6, 46) * mm});
            skSolve(sketch);
        }
        {
            var Q0;
            Q0=makeQuery(id+"F12.imprint","IMPRINT",FACE,{"disambiguationData":[TD([[makeQuery(id+"F12.imprint","IMPRINT",EDGE,{"derivedFrom":sQuery(id+"F12.wireOp",EDGE,"E42")}),1.0]])]});
            extrude(context, id + "F13", {"entities" : qUnion([Q0]), "operationType" : NewBodyOperationType.ADD, "depth" : 2 * mm, "offsetDistance" : 25 * mm});
        }
        {
            var Q0;
            Q0=makeQuery(id+"F13.opExtrude","CAP_EDGE",EDGE,{"disambiguationData":[OSD([sQuery(id+"F12.wireOp",EDGE,"E45")])],"isStart":false});
            chamfer(context, id + "F14", {"entities" : qUnion([Q0]), "width" : 2 * mm, "tangentPropagation" : true});
        }
        {
            var Q0;
            Q0=makeQuery(id+"F13.boolean.opBoolean","MERGE",FACE,{"derivedFrom":[makeQuery(id+"F10.boolean.opBoolean","MERGE",FACE,{"derivedFrom":[makeQuery(id+"F7.boolean.opBoolean","MERGE",FACE,{"derivedFrom":[makeQuery(id+"F4.boolean.opBoolean","MERGE",FACE,{"derivedFrom":[makeQuery(id+"F1.opExtrude","CAP_FACE",FACE,{"disambiguationData":[OSD([sQuery(id+"F0.wireOp",EDGE,"E0.bottom"),sQuery(id+"F0.wireOp",EDGE,"E0.top"),sQuery(id+"F0.wireOp",EDGE,"E0.left"),sQuery(id+"F0.wireOp",EDGE,"E0.right"),sQuery(id+"F0.wireOp",EDGE,"E4"),sQuery(id+"F0.wireOp",EDGE,"E5"),sQuery(id+"F0.wireOp",EDGE,"E6"),sQuery(id+"F0.wireOp",EDGE,"E7"),sQuery(id+"F0.wireOp",EDGE,"E11.0.1.1"),sQuery(id+"F0.wireOp",EDGE,"E11.0.1.2"),sQuery(id+"F0.wireOp",EDGE,"E11.0.1.3"),sQuery(id+"F0.wireOp",EDGE,"E11.0.1.6"),sQuery(id+"F0.wireOp",EDGE,"E11.0.2.1"),sQuery(id+"F0.wireOp",EDGE,"E11.0.2.2"),sQuery(id+"F0.wireOp",EDGE,"E11.0.2.3"),sQuery(id+"F0.wireOp",EDGE,"E11.0.2.6"),sQuery(id+"F0.wireOp",EDGE,"E11.0.3.1"),sQuery(id+"F0.wireOp",EDGE,"E11.0.3.2"),sQuery(id+"F0.wireOp",EDGE,"E11.0.3.3"),sQuery(id+"F0.wireOp",EDGE,"E11.0.3.6"),sQuery(id+"F0.wireOp",EDGE,"E11.0.4.1"),sQuery(id+"F0.wireOp",EDGE,"E11.0.4.2"),sQuery(id+"F0.wireOp",EDGE,"E11.0.4.3"),sQuery(id+"F0.wireOp",EDGE,"E11.0.4.6"),sQuery(id+"F0.wireOp",EDGE,"E11.1.0.1"),sQuery(id+"F0.wireOp",EDGE,"E11.1.0.2"),sQuery(id+"F0.wireOp",EDGE,"E11.1.0.3"),sQuery(id+"F0.wireOp",EDGE,"E11.1.0.6"),sQuery(id+"F0.wireOp",EDGE,"E11.1.1.1"),sQuery(id+"F0.wireOp",EDGE,"E11.1.1.2"),sQuery(id+"F0.wireOp",EDGE,"E11.1.1.3"),sQuery(id+"F0.wireOp",EDGE,"E11.1.1.6"),sQuery(id+"F0.wireOp",EDGE,"E11.1.2.1"),sQuery(id+"F0.wireOp",EDGE,"E11.1.2.2"),sQuery(id+"F0.wireOp",EDGE,"E11.1.2.3"),sQuery(id+"F0.wireOp",EDGE,"E11.1.2.6"),sQuery(id+"F0.wireOp",EDGE,"E11.1.3.1"),sQuery(id+"F0.wireOp",EDGE,"E11.1.3.2"),sQuery(id+"F0.wireOp",EDGE,"E11.1.3.3"),sQuery(id+"F0.wireOp",EDGE,"E11.1.3.6"),sQuery(id+"F0.wireOp",EDGE,"E11.1.4.1"),sQuery(id+"F0.wireOp",EDGE,"E11.1.4.2"),sQuery(id+"F0.wireOp",EDGE,"E11.1.4.3"),sQuery(id+"F0.wireOp",EDGE,"E11.1.4.6"),sQuery(id+"F0.wireOp",EDGE,"E11.2.0.1"),sQuery(id+"F0.wireOp",EDGE,"E11.2.0.2"),sQuery(id+"F0.wireOp",EDGE,"E11.2.0.3"),sQuery(id+"F0.wireOp",EDGE,"E11.2.0.6"),sQuery(id+"F0.wireOp",EDGE,"E11.2.1.1"),sQuery(id+"F0.wireOp",EDGE,"E11.2.1.2"),sQuery(id+"F0.wireOp",EDGE,"E11.2.1.3"),sQuery(id+"F0.wireOp",EDGE,"E11.2.1.6"),sQuery(id+"F0.wireOp",EDGE,"E11.2.2.1"),sQuery(id+"F0.wireOp",EDGE,"E11.2.2.2"),sQuery(id+"F0.wireOp",EDGE,"E11.2.2.3"),sQuery(id+"F0.wireOp",EDGE,"E11.2.2.6"),sQuery(id+"F0.wireOp",EDGE,"E11.2.3.1"),sQuery(id+"F0.wireOp",EDGE,"E11.2.3.2"),sQuery(id+"F0.wireOp",EDGE,"E11.2.3.3"),sQuery(id+"F0.wireOp",EDGE,"E11.2.3.6"),sQuery(id+"F0.wireOp",EDGE,"E11.2.4.1"),sQuery(id+"F0.wireOp",EDGE,"E11.2.4.2"),sQuery(id+"F0.wireOp",EDGE,"E11.2.4.3"),sQuery(id+"F0.wireOp",EDGE,"E11.2.4.6"),sQuery(id+"F0.wireOp",EDGE,"E11.3.0.1"),sQuery(id+"F0.wireOp",EDGE,"E11.3.0.2"),sQuery(id+"F0.wireOp",EDGE,"E11.3.0.3"),sQuery(id+"F0.wireOp",EDGE,"E11.3.0.6"),sQuery(id+"F0.wireOp",EDGE,"E11.3.1.1"),sQuery(id+"F0.wireOp",EDGE,"E11.3.1.2"),sQuery(id+"F0.wireOp",EDGE,"E11.3.1.3"),sQuery(id+"F0.wireOp",EDGE,"E11.3.1.6"),sQuery(id+"F0.wireOp",EDGE,"E11.3.2.1"),sQuery(id+"F0.wireOp",EDGE,"E11.3.2.2"),sQuery(id+"F0.wireOp",EDGE,"E11.3.2.3"),sQuery(id+"F0.wireOp",EDGE,"E11.3.2.6"),sQuery(id+"F0.wireOp",EDGE,"E11.3.3.1"),sQuery(id+"F0.wireOp",EDGE,"E11.3.3.2"),sQuery(id+"F0.wireOp",EDGE,"E11.3.3.3"),sQuery(id+"F0.wireOp",EDGE,"E11.3.3.6"),sQuery(id+"F0.wireOp",EDGE,"E11.3.4.1"),sQuery(id+"F0.wireOp",EDGE,"E11.3.4.2"),sQuery(id+"F0.wireOp",EDGE,"E11.3.4.3"),sQuery(id+"F0.wireOp",EDGE,"E11.3.4.6"),sQuery(id+"F0.wireOp",EDGE,"E11.4.0.1"),sQuery(id+"F0.wireOp",EDGE,"E11.4.0.2"),sQuery(id+"F0.wireOp",EDGE,"E11.4.0.3"),sQuery(id+"F0.wireOp",EDGE,"E11.4.0.6"),sQuery(id+"F0.wireOp",EDGE,"E11.4.1.1"),sQuery(id+"F0.wireOp",EDGE,"E11.4.1.2"),sQuery(id+"F0.wireOp",EDGE,"E11.4.1.3"),sQuery(id+"F0.wireOp",EDGE,"E11.4.1.6"),sQuery(id+"F0.wireOp",EDGE,"E11.4.2.1"),sQuery(id+"F0.wireOp",EDGE,"E11.4.2.2"),sQuery(id+"F0.wireOp",EDGE,"E11.4.2.3"),sQuery(id+"F0.wireOp",EDGE,"E11.4.2.6"),sQuery(id+"F0.wireOp",EDGE,"E11.4.3.1"),sQuery(id+"F0.wireOp",EDGE,"E11.4.3.2"),sQuery(id+"F0.wireOp",EDGE,"E11.4.3.3"),sQuery(id+"F0.wireOp",EDGE,"E11.4.3.6"),sQuery(id+"F0.wireOp",EDGE,"E11.4.4.1"),sQuery(id+"F0.wireOp",EDGE,"E11.4.4.2"),sQuery(id+"F0.wireOp",EDGE,"E11.4.4.3"),sQuery(id+"F0.wireOp",EDGE,"E11.4.4.6")])],"isStart":false}),makeQuery(id+"F4.opExtrude","SWEPT_FACE",FACE,{"disambiguationData":[OSD([sQuery(id+"F3.wireOp",EDGE,"E28")])]})]}),makeQuery(id+"F7.opExtrude","SWEPT_FACE",FACE,{"disambiguationData":[OSD([sQuery(id+"F6.wireOp",EDGE,"E34")])]})]}),makeQuery(id+"F10.opExtrude","SWEPT_FACE",FACE,{"disambiguationData":[OSD([sQuery(id+"F9.wireOp",EDGE,"E37")])]})]}),makeQuery(id+"F13.opExtrude","SWEPT_FACE",FACE,{"disambiguationData":[OSD([sQuery(id+"F12.wireOp",EDGE,"E42")])]})]});
            var sketch = newSketch(context, id + "F15", { "sketchPlane" : qUnion([Q0])});
            skLineSegment(sketch, "E48", {"start": v(-62.6, 62.6) * mm, "end": v(-62.6, -62.6) * mm});
            skLineSegment(sketch, "E49", {"start": v(-62.6, -62.6) * mm, "end": v(62.6, -62.6) * mm});
            skLineSegment(sketch, "E50", {"start": v(62.6, -62.6) * mm, "end": v(62.6, 62.6) * mm});
            skLineSegment(sketch, "E51", {"start": v(62.6, 62.6) * mm, "end": v(-62.6, 62.6) * mm});
            skLineSegment(sketch, "E52.0", {"start": v(61.1, 61.1) * mm, "end": v(-61.1, 61.1) * mm});
            skLineSegment(sketch, "E52.1", {"start": v(61.1, -61.1) * mm, "end": v(61.1, 61.1) * mm});
            skLineSegment(sketch, "E52.2", {"start": v(-61.1, -61.1) * mm, "end": v(61.1, -61.1) * mm});
            skLineSegment(sketch, "E52.3", {"start": v(-61.1, 61.1) * mm, "end": v(-61.1, -61.1) * mm});
            skSolve(sketch);
        }
        {
            var Q0;
            Q0=makeQuery(id+"F15.imprint","IMPRINT",FACE,{"disambiguationData":[TD([[makeQuery(id+"F15.imprint","IMPRINT",EDGE,{"derivedFrom":sQuery(id+"F15.wireOp",EDGE,"E48")}),1.0]])]});
            extrude(context, id + "F16", {"entities" : qUnion([Q0]), "operationType" : NewBodyOperationType.ADD, "depth" : 4 * mm, "offsetDistance" : 25 * mm});
        }
    });
